# Revit family: 121511001_Sanitario Fussion Alongado
name_source: partatom
category: Plumbing Fixtures
units: mm (PartAtom-declared; Revit-internal decimal feet)

## family parameters
Always vertical = Yes
Cut with Voids When Loaded = No
Host = Wall
OmniClass Number = 23.31.19.17
Part Type = Normal
Room Calculation Point = No
Round Connector Dimension = Use Diameter
Shared = No

## types (1)
- Type 1
    Altura de sello = 51 mm. - 2,0 pulg.
    Ancho = 350 mm  [stored 1.14829 ft]
    Capacidad de descarga = 350 gr
    Consumo de agua = Consumo de 6,0 Lpf - 1,6 gpf para so lidos y 4.0 Lpf - 1,0 gpf para liquidos.
    Creado por = BIMBAU
    Default Elevation = 0 mm  [stored 0 ft]
    Description = "Disfruta en tu baño del sanitario Fussion de diseño moderno con geometrías básicas y sifón oculto, que te permitirá una mejor limpieza."
    Espejo de agua = 125 x 100 mm. - 4,9 x 3,9 pulg.
    Fecha de creación = 12/03/2021
    Manufacturer = Corona
    Material = Corona_Porcelana_Vitrea
    Model = Sanitario fussion alongado
    Peso Bruto aprox = 37,9 kg. - 83,6 lbs
    Peso Neto aprox = 37,4 kg. - 82,4 lbs
    Presión de agua = 20 - 80 PSI
    Profundidad = 680 mm  [stored 2.23097 ft]
    Sistema de descarga = Variable
    URL = https://corona.co

note: [stored X ft] marks values corroborated as IEEE doubles in the binary element streams (Revit-internal decimal feet)

## geometry (parser evidence)
native form markers: Sweep x7
no freeform markers — native parametric forms only
